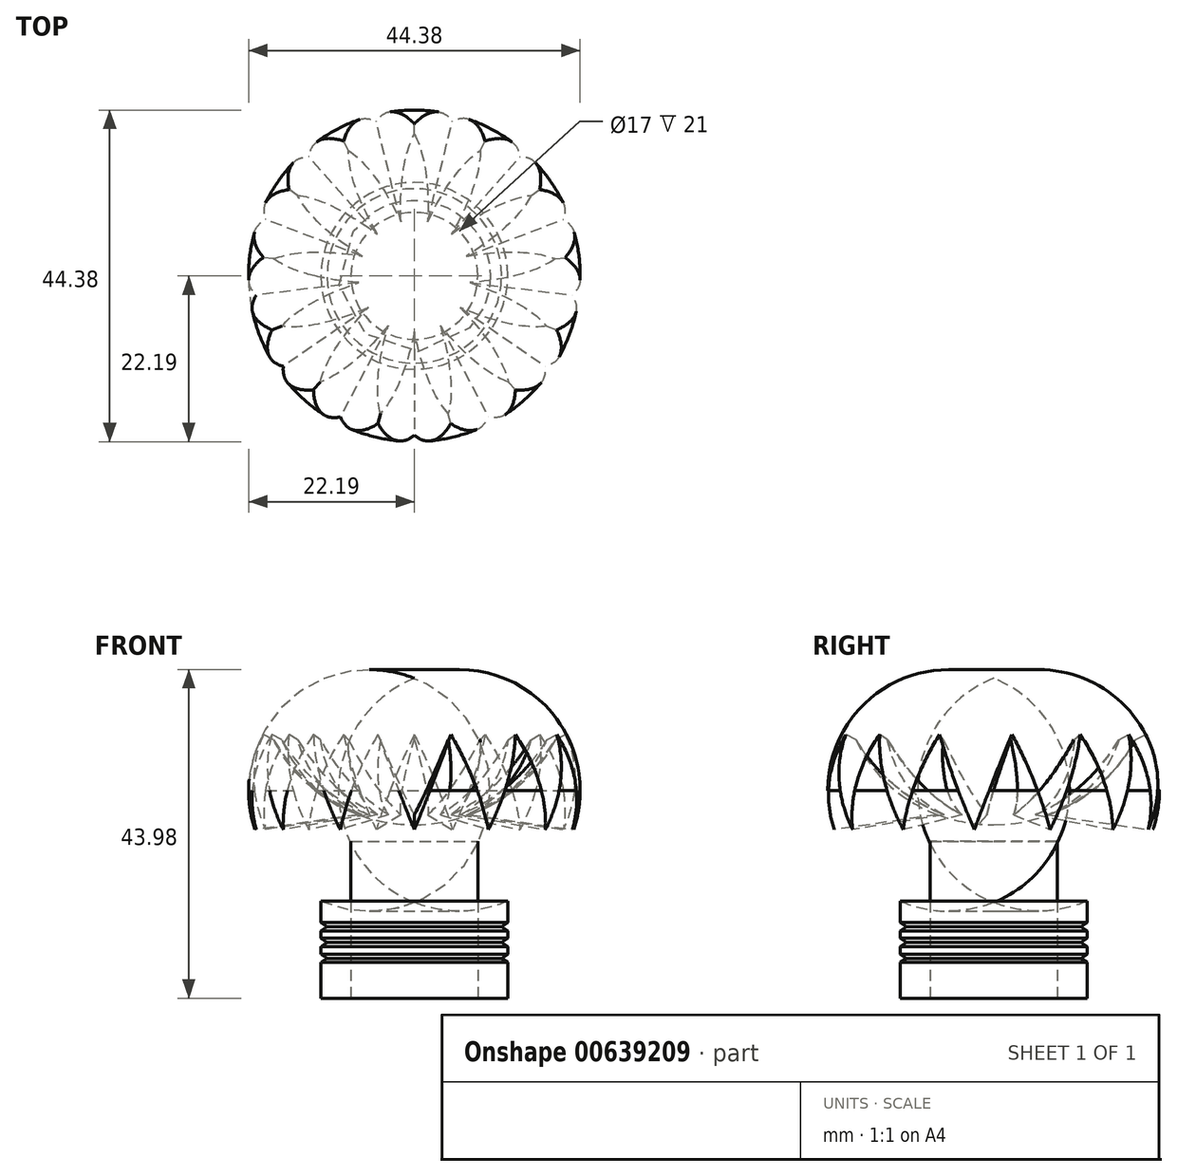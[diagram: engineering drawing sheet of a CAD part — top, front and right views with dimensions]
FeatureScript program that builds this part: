
annotation { "Feature Type Name" : "Feature", "Feature Type Description" : "" }
export const myFeature = defineFeature(function(context is Context, id is Id, definition is map)
    precondition{}
    {
        {
            var Q0;
            Q0=qCreatedBy(makeId("Front.planeOp"),FACE);
            var sketch = newSketch(context, id + "F0", { "sketchPlane" : qUnion([Q0])});
            skLineSegment(sketch, "E0", {"start": v(0, 0) * mm, "end": v(0, 21) * mm});
            skLineSegment(sketch, "E1", {"start": v(0, 21) * mm, "end": v(-8.5, 21) * mm});
            skLineSegment(sketch, "E2", {"start": v(-8.5, 0) * mm, "end": v(-12.5, 0) * mm});
            skLineSegment(sketch, "E3", {"start": v(-12.5, 0) * mm, "end": v(-12.5, 4.78) * mm});
            skArc(sketch, "E4", {"start": v(-20.33, 35.33) * mm, "mid": v(-21.27, 22.46) * mm, "end": v(-12.5, 13) * mm});
            skLineSegment(sketch, "E5", {"start": v(-20.33, 35.33) * mm, "end": v(-19.33, 35.33) * mm});
            skArc(sketch, "E6", {"start": v(-19.33, 35.33) * mm, "mid": v(-11.4, 26.5) * mm, "end": v(0, 23.21) * mm});
            skLineSegment(sketch, "E7", {"start": v(-12.5, 4.78) * mm, "end": v(-11.67, 5.34) * mm});
            skLineSegment(sketch, "E8", {"start": v(-11.67, 5.34) * mm, "end": v(-12.5, 5.9) * mm});
            skLineSegment(sketch, "E9", {"start": v(-12.5, 5.9) * mm, "end": v(-12.5, 6.9) * mm});
            skLineSegment(sketch, "E10", {"start": v(-12.5, 6.9) * mm, "end": v(-11.67, 7.45) * mm});
            skLineSegment(sketch, "E11", {"start": v(-11.67, 7.45) * mm, "end": v(-12.5, 8.01) * mm});
            skLineSegment(sketch, "E12", {"start": v(-12.5, 8.01) * mm, "end": v(-12.5, 9) * mm});
            skLineSegment(sketch, "E13", {"start": v(-12.5, 9) * mm, "end": v(-11.67, 9.57) * mm});
            skLineSegment(sketch, "E14", {"start": v(-11.67, 9.57) * mm, "end": v(-12.5, 10.13) * mm});
            skLineSegment(sketch, "E15", {"start": v(-12.5, 10.13) * mm, "end": v(-12.5, 11.12) * mm});
            skLineSegment(sketch, "E16", {"start": v(-8.5, 21) * mm, "end": v(-8.5, 0) * mm});
            skLineSegment(sketch, "E17.trimOffspring", {"start": v(-12.5, 10.13) * mm, "end": v(-12.5, 13) * mm});
            skLineSegment(sketch, "E18", {"start": v(0, 23.21) * mm, "end": v(0, 21) * mm});
            skSolve(sketch);
        }
        {
            var Q0;
            Q0=makeQuery(id+"F0.imprint","IMPRINT",FACE,{"disambiguationData":[TD([[makeQuery(id+"F0.imprint","IMPRINT",EDGE,{"derivedFrom":sQuery(id+"F0.wireOp",EDGE,"E1")}),-1.0]])]});
            var Q1;
            Q1=sQuery(id+"F0.wireOp",EDGE,"E0");
            revolve(context, id + "F1", {"entities" : qUnion([Q0]), "axis" : qUnion([Q1]), "revolveType" : RevolveType.FULL});
        }
        {
            var Q0;
            Q0=qCreatedBy(makeId("Front.planeOp"),FACE);
            var sketch = newSketch(context, id + "F2", { "sketchPlane" : qUnion([Q0])});
            skLineSegment(sketch, "E19", {"start": v(0, 35.88) * mm, "end": v(4, 35.88) * mm});
            skLineSegment(sketch, "E20", {"start": v(4, 35.88) * mm, "end": v(0, 25.63) * mm});
            skLineSegment(sketch, "E21.MirrorCS", {"start": v(0, 35.88) * mm, "end": v(-4, 35.88) * mm});
            skLineSegment(sketch, "E22.MirrorCS", {"start": v(-4, 35.88) * mm, "end": v(0, 25.63) * mm});
            skSolve(sketch);
        }
        {
            var Q0;
            Q0 = qSketchRegion(id + "F2", true);
            extrude(context, id + "F3", {"entities" : qUnion([Q0]), "endBound" : BoundingType.THROUGH_ALL, "depth" : 25 * mm, "offsetDistance" : 25 * mm, "hasDraft" : true, "draftAngle" : 3 * degree});
        }
        {
            var Q0;
            Q0=makeQuery(id+"F3.opExtrude","SWEPT_BODY",BODY,{"disambiguationData":[OSD([sQuery(id+"F2.wireOp",EDGE,"E19"),sQuery(id+"F2.wireOp",EDGE,"E20"),sQuery(id+"F2.wireOp",EDGE,"E21.MirrorCS"),sQuery(id+"F2.wireOp",EDGE,"E22.MirrorCS")])]});
            var Q1;
            Q1=makeQuery(id+"F1.opRevolve","SWEPT_FACE",FACE,{"disambiguationData":[OSD([sQuery(id+"F0.wireOp",EDGE,"E17.trimOffspring")])]});
            circularPattern(context, id + "F4", {"operationType" : NewBodyOperationType.REMOVE, "entities" : qUnion([Q0]), "axis" : qUnion([Q1]), "angle" : 360 * degree, "instanceCount" : 13, "equalSpace" : true});
        }
    });
